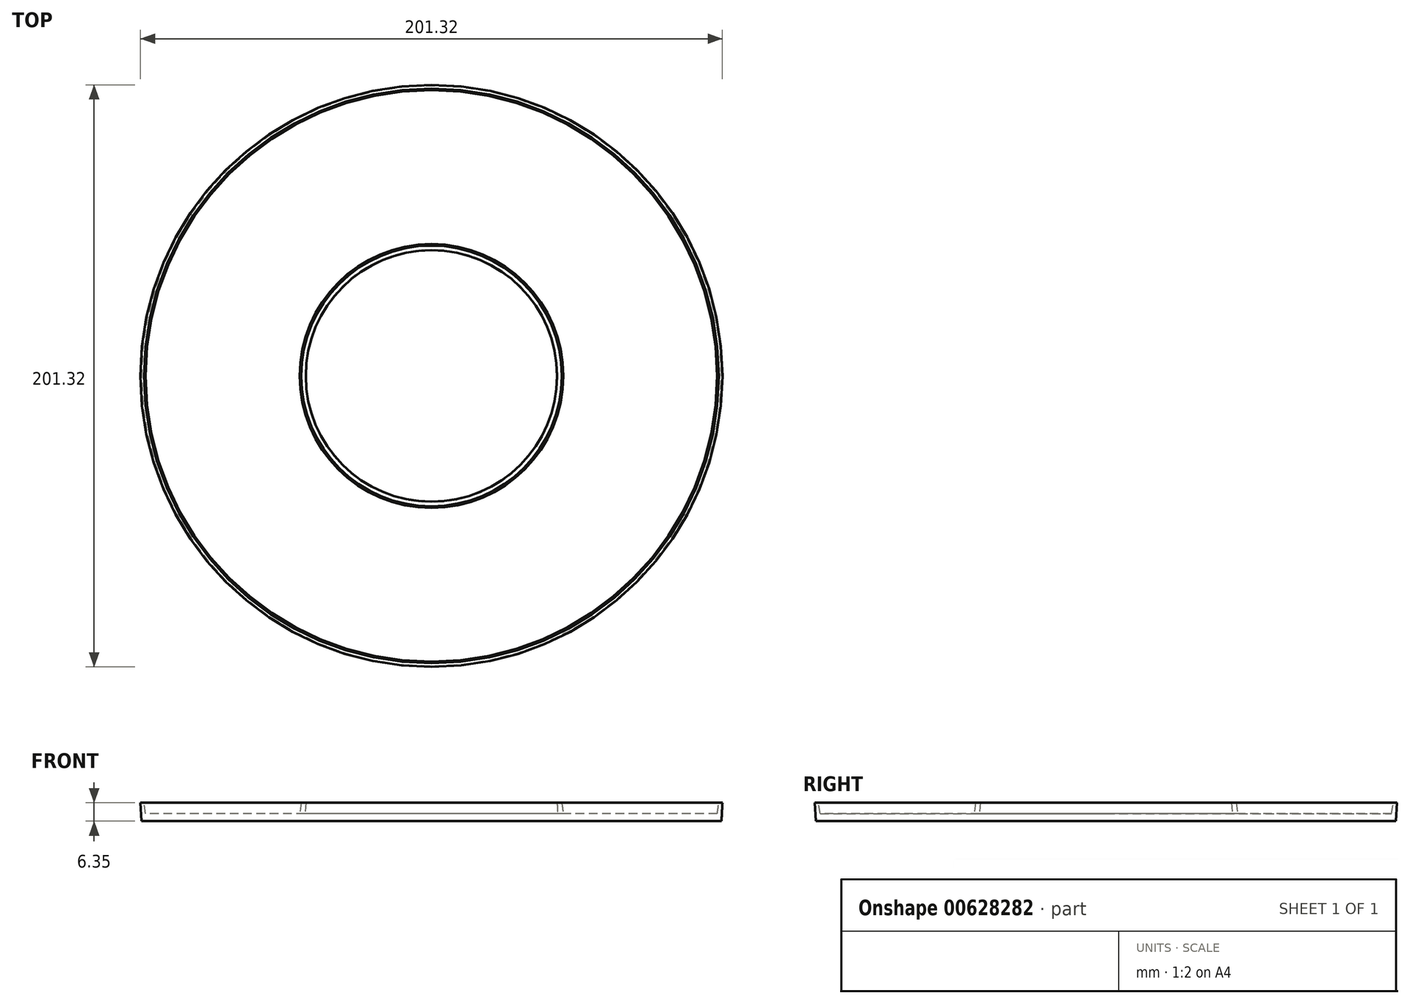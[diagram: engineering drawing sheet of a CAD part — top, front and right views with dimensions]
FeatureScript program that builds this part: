
annotation { "Feature Type Name" : "Feature", "Feature Type Description" : "" }
export const myFeature = defineFeature(function(context is Context, id is Id, definition is map)
    precondition{}
    {
        {
            var Q0;
            Q0=qCreatedBy(makeId("Top.planeOp"),FACE);
            var sketch = newSketch(context, id + "F0", { "sketchPlane" : qUnion([Q0])});
            skCircle(sketch, "E0", {"center": v(0, 0) * mm, "radius": 100.33 * mm});
            skCircle(sketch, "E1", {"center": v(0, 0) * mm, "radius": 43.82 * mm});
            skSolve(sketch);
        }
        {
            var Q0;
            Q0=makeQuery(id+"F0.imprint","IMPRINT",FACE,{"disambiguationData":[TD([[makeQuery(id+"F0.imprint","IMPRINT",EDGE,{"derivedFrom":sQuery(id+"F0.wireOp",EDGE,"E0")}),1.0]])]});
            extrude(context, id + "F1", {"entities" : qUnion([Q0]), "depth" : 6.35 * mm, "offsetDistance" : 25.4 * mm, "hasDraft" : true, "draftAngle" : 3 * degree});
        }
        {
            var Q0;
            Q0=makeQuery(id+"F0.imprint","IMPRINT",FACE,{"disambiguationData":[TD([[makeQuery(id+"F0.imprint","IMPRINT",EDGE,{"derivedFrom":sQuery(id+"F0.wireOp",EDGE,"E1")}),1.0]])]});
            extrude(context, id + "F2", {"entities" : qUnion([Q0]), "operationType" : NewBodyOperationType.ADD, "depth" : 2.54 * mm, "offsetDistance" : 25.4 * mm});
        }
        {
            var Q0;
            Q0=makeQuery(id+"F1.opExtrude","CAP_FACE",FACE,{"disambiguationData":[OSD([sQuery(id+"F0.wireOp",EDGE,"E0"),sQuery(id+"F0.wireOp",EDGE,"E1")])],"isStart":false});
            var sketch = newSketch(context, id + "F3", { "sketchPlane" : qUnion([Q0])});
            skCircle(sketch, "E2", {"center": v(0, 0) * mm, "radius": 43.82 * mm});
            skCircle(sketch, "E3", {"center": v(0, 0) * mm, "radius": 45.09 * mm});
            skCircle(sketch, "E4", {"center": v(0, 0) * mm, "radius": 99.4 * mm});
            skSolve(sketch);
        }
        {
            var Q0;
            Q0=makeQuery(id+"F3.imprint","IMPRINT",FACE,{"disambiguationData":[TD([[makeQuery(id+"F3.imprint","IMPRINT",EDGE,{"derivedFrom":makeQuery(id+"F1.opExtrude","CAP_EDGE",EDGE,{"disambiguationData":[OSD([sQuery(id+"F0.wireOp",EDGE,"E1")])],"isStart":false})}),1.0]])]});
            var Q1;
            Q1=makeQuery(id+"F2.opExtrude","CAP_FACE",FACE,{"disambiguationData":[OSD([sQuery(id+"F0.wireOp",EDGE,"E1")])],"isStart":false});
            extrude(context, id + "F4", {"entities" : qUnion([Q0]), "operationType" : NewBodyOperationType.REMOVE, "endBound" : BoundingType.UP_TO_SURFACE, "oppositeDirection" : true, "depth" : 25.4 * mm, "endBoundEntityFace" : qUnion([Q1]), "offsetDistance" : 25.4 * mm});
        }
        {
            var Q0;
            Q0=makeQuery(id+"F3.imprint","IMPRINT",FACE,{"disambiguationData":[TD([[makeQuery(id+"F3.imprint","IMPRINT",EDGE,{"derivedFrom":sQuery(id+"F3.wireOp",EDGE,"E3")}),-1.0]])]});
            var Q1;
            Q1=makeQuery(id+"F2.opExtrude","CAP_FACE",FACE,{"disambiguationData":[OSD([sQuery(id+"F0.wireOp",EDGE,"E1")])],"isStart":false});
            extrude(context, id + "F5", {"entities" : qUnion([Q0]), "operationType" : NewBodyOperationType.REMOVE, "endBound" : BoundingType.UP_TO_SURFACE, "oppositeDirection" : true, "depth" : 25.4 * mm, "endBoundEntityFace" : qUnion([Q1]), "offsetDistance" : 25.4 * mm, "hasDraft" : true, "draftAngle" : 8 * degree, "draftPullDirection" : true});
        }
    });
